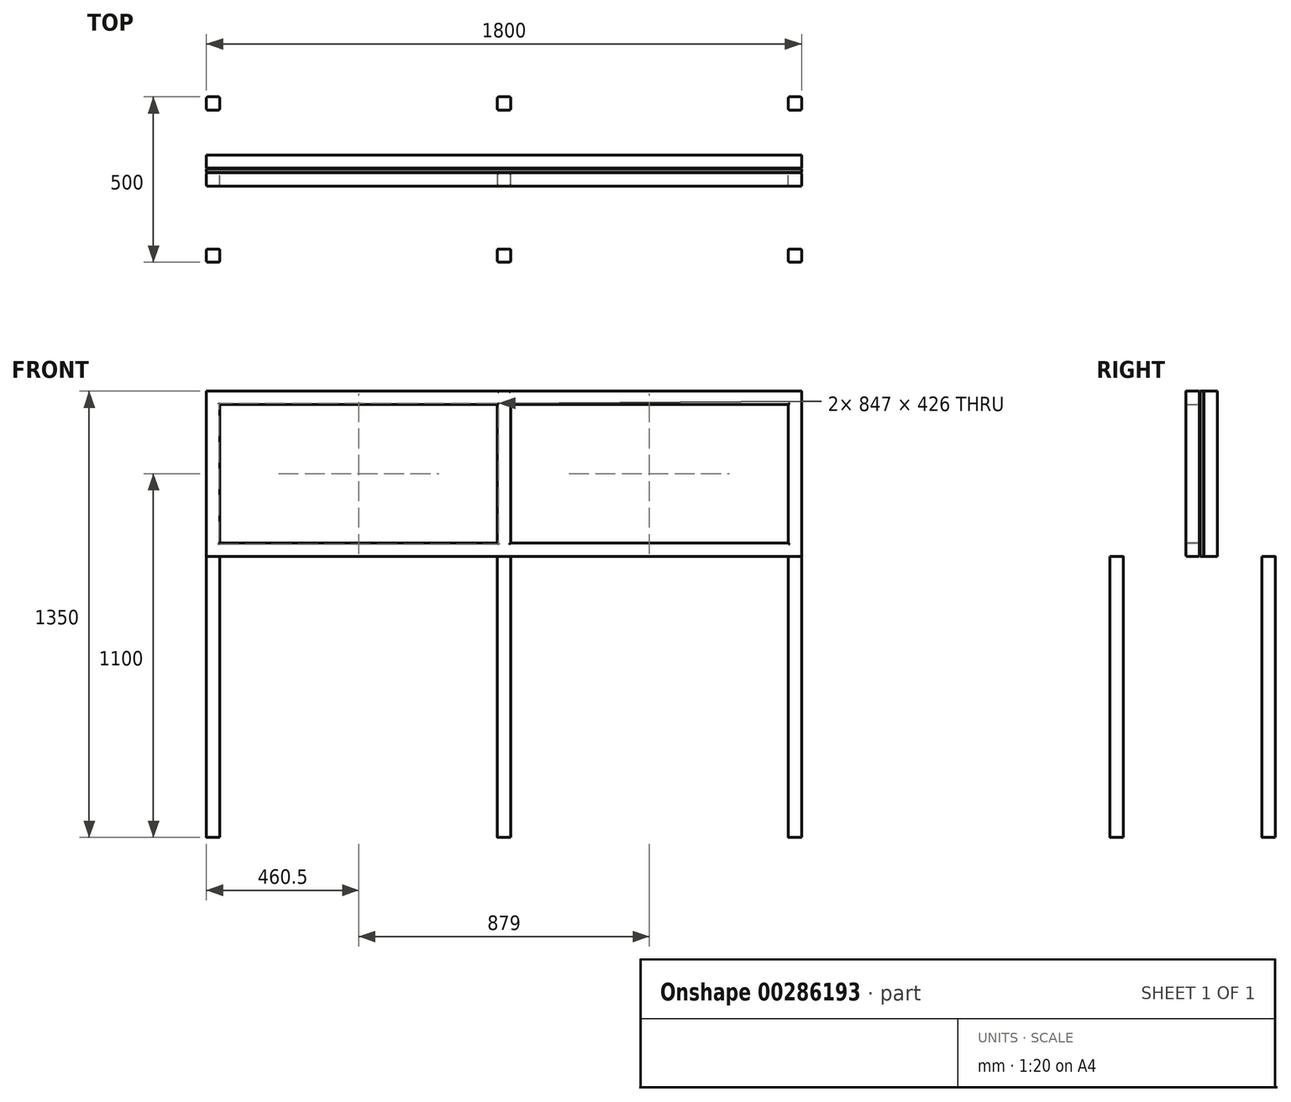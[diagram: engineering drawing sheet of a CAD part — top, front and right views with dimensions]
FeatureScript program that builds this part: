
annotation { "Feature Type Name" : "Feature", "Feature Type Description" : "" }
export const myFeature = defineFeature(function(context is Context, id is Id, definition is map)
    precondition{}
    {
        {
            var Q0;
            Q0=qCreatedBy(makeId("Front.planeOp"),FACE);
            var sketch = newSketch(context, id + "F6", { "sketchPlane" : qUnion([Q0])});
            skLineSegment(sketch, "E0.bottom", {"start": v(880, -230) * mm, "end": v(-880, -230) * mm});
            skLineSegment(sketch, "E0.top", {"start": v(880, 230) * mm, "end": v(-880, 230) * mm});
            skLineSegment(sketch, "E0.left", {"start": v(880, -230) * mm, "end": v(880, 230) * mm});
            skLineSegment(sketch, "E0.right", {"start": v(-880, -230) * mm, "end": v(-880, 230) * mm});
            skPoint(sketch, "E0.middle", {"position": v(0, 0) * mm});
            skLineSegment(sketch, "E1", {"start": v(0, 230) * mm, "end": v(0, -230) * mm});
            skSolve(sketch);
        }
        {
            var Q0;
            Q0=qCreatedBy(makeId("Right.planeOp"),FACE);
            var sketch = newSketch(context, id + "F0", { "sketchPlane" : qUnion([Q0])});
            skLineSegment(sketch, "E2.bottom", {"start": v(17, -250) * mm, "end": v(-17, -250) * mm});
            skLineSegment(sketch, "E2.top", {"start": v(17, -210) * mm, "end": v(-17, -210) * mm});
            skLineSegment(sketch, "E2.left", {"start": v(20, -247) * mm, "end": v(20, -213) * mm});
            skLineSegment(sketch, "E2.right", {"start": v(-20, -247) * mm, "end": v(-20, -213) * mm});
            skPoint(sketch, "E2.middle", {"position": v(0, -230) * mm});
            skPoint(sketch, "E3.visualSharp", {"position": v(20, -210) * mm});
            skArc(sketch, "E3.filletArc", {"start": v(20, -213) * mm, "mid": v(19.12, -210.88) * mm, "end": v(17, -210) * mm});
            skPoint(sketch, "E4.visualSharp", {"position": v(-20, -210) * mm});
            skArc(sketch, "E4.filletArc", {"start": v(-17, -210) * mm, "mid": v(-19.12, -210.88) * mm, "end": v(-20, -213) * mm});
            skPoint(sketch, "E5.visualSharp", {"position": v(20, -250) * mm});
            skArc(sketch, "E5.filletArc", {"start": v(17, -250) * mm, "mid": v(19.12, -249.12) * mm, "end": v(20, -247) * mm});
            skPoint(sketch, "E6.visualSharp", {"position": v(-20, -250) * mm});
            skArc(sketch, "E6.filletArc", {"start": v(-20, -247) * mm, "mid": v(-19.12, -249.12) * mm, "end": v(-17, -250) * mm});
            skSolve(sketch);
        }
        {
            var Q0;
            Q0=makeQuery(id+"F0.imprint","IMPRINT",FACE,{"disambiguationData":[TD([[makeQuery(id+"F0.imprint","IMPRINT",EDGE,{"derivedFrom":sQuery(id+"F0.wireOp",EDGE,"E2.bottom")}),-1.0]])]});
            var Q1;
            Q1=sQuery(id+"F6.wireOp",EDGE,"E0.right");
            var Q2;
            Q2=sQuery(id+"F6.wireOp",EDGE,"E0.top");
            var Q3;
            Q3=sQuery(id+"F6.wireOp",EDGE,"E0.bottom");
            var Q4;
            Q4=sQuery(id+"F6.wireOp",EDGE,"E0.left");
            sweep(context, id + "F7", {"profiles" : qUnion([Q0]), "path" : qUnion([Q1, Q2, Q3, Q4])});
        }
        {
            var Q0;
            Q0=makeQuery(id+"F7.opSweep","SWEPT_FACE",FACE,{"disambiguationData":[OSD([sQuery(id+"F6.wireOp",EDGE,"E0.bottom"),sQuery(id+"F0.wireOp",EDGE,"E2.right")])]});
            var sketch = newSketch(context, id + "F8", { "sketchPlane" : qUnion([Q0])});
            skLineSegment(sketch, "E7.bottom", {"start": v(864, 210) * mm, "end": v(896, 210) * mm});
            skLineSegment(sketch, "E7.top", {"start": v(864, 250) * mm, "end": v(896, 250) * mm});
            skLineSegment(sketch, "E7.left", {"start": v(860, 214) * mm, "end": v(860, 246) * mm});
            skLineSegment(sketch, "E7.right", {"start": v(900, 214) * mm, "end": v(900, 246) * mm});
            skPoint(sketch, "E8.visualSharp", {"position": v(900, 250) * mm});
            skArc(sketch, "E8.filletArc", {"start": v(900, 246) * mm, "mid": v(898.83, 248.83) * mm, "end": v(896, 250) * mm});
            skPoint(sketch, "E9.visualSharp", {"position": v(860, 250) * mm});
            skArc(sketch, "E9.filletArc", {"start": v(864, 250) * mm, "mid": v(861.17, 248.83) * mm, "end": v(860, 246) * mm});
            skPoint(sketch, "E10.visualSharp", {"position": v(860, 210) * mm});
            skArc(sketch, "E10.filletArc", {"start": v(860, 214) * mm, "mid": v(861.17, 211.17) * mm, "end": v(864, 210) * mm});
            skPoint(sketch, "E11.visualSharp", {"position": v(900, 210) * mm});
            skArc(sketch, "E11.filletArc", {"start": v(896, 210) * mm, "mid": v(898.83, 211.17) * mm, "end": v(900, 214) * mm});
            skArc(sketch, "E12.0.1.0", {"start": v(896, -250) * mm, "mid": v(898.83, -248.83) * mm, "end": v(900, -246) * mm});
            skArc(sketch, "E12.0.1.1", {"start": v(864, -210) * mm, "mid": v(861.17, -211.17) * mm, "end": v(860, -214) * mm});
            skLineSegment(sketch, "E12.0.1.2", {"start": v(860, -246) * mm, "end": v(860, -214) * mm});
            skArc(sketch, "E12.0.1.3", {"start": v(900, -214) * mm, "mid": v(898.83, -211.17) * mm, "end": v(896, -210) * mm});
            skLineSegment(sketch, "E12.0.1.4", {"start": v(864, -250) * mm, "end": v(896, -250) * mm});
            skLineSegment(sketch, "E12.0.1.5", {"start": v(864, -210) * mm, "end": v(896, -210) * mm});
            skArc(sketch, "E12.0.1.6", {"start": v(860, -246) * mm, "mid": v(861.17, -248.83) * mm, "end": v(864, -250) * mm});
            skLineSegment(sketch, "E12.0.1.7", {"start": v(900, -246) * mm, "end": v(900, -214) * mm});
            skArc(sketch, "E12.1.0.0", {"start": v(16, 210) * mm, "mid": v(18.83, 211.17) * mm, "end": v(20, 214) * mm});
            skArc(sketch, "E12.1.0.1", {"start": v(-16, 250) * mm, "mid": v(-18.83, 248.83) * mm, "end": v(-20, 246) * mm});
            skLineSegment(sketch, "E12.1.0.2", {"start": v(-20, 214) * mm, "end": v(-20, 246) * mm});
            skArc(sketch, "E12.1.0.3", {"start": v(20, 246) * mm, "mid": v(18.83, 248.83) * mm, "end": v(16, 250) * mm});
            skLineSegment(sketch, "E12.1.0.4", {"start": v(-16, 210) * mm, "end": v(16, 210) * mm});
            skLineSegment(sketch, "E12.1.0.5", {"start": v(-16, 250) * mm, "end": v(16, 250) * mm});
            skArc(sketch, "E12.1.0.6", {"start": v(-20, 214) * mm, "mid": v(-18.83, 211.17) * mm, "end": v(-16, 210) * mm});
            skLineSegment(sketch, "E12.1.0.7", {"start": v(20, 214) * mm, "end": v(20, 246) * mm});
            skArc(sketch, "E12.1.1.0", {"start": v(16, -250) * mm, "mid": v(18.83, -248.83) * mm, "end": v(20, -246) * mm});
            skArc(sketch, "E12.1.1.1", {"start": v(-16, -210) * mm, "mid": v(-18.83, -211.17) * mm, "end": v(-20, -214) * mm});
            skLineSegment(sketch, "E12.1.1.2", {"start": v(-20, -246) * mm, "end": v(-20, -214) * mm});
            skArc(sketch, "E12.1.1.3", {"start": v(20, -214) * mm, "mid": v(18.83, -211.17) * mm, "end": v(16, -210) * mm});
            skLineSegment(sketch, "E12.1.1.4", {"start": v(-16, -250) * mm, "end": v(16, -250) * mm});
            skLineSegment(sketch, "E12.1.1.5", {"start": v(-16, -210) * mm, "end": v(16, -210) * mm});
            skArc(sketch, "E12.1.1.6", {"start": v(-20, -246) * mm, "mid": v(-18.83, -248.83) * mm, "end": v(-16, -250) * mm});
            skLineSegment(sketch, "E12.1.1.7", {"start": v(20, -246) * mm, "end": v(20, -214) * mm});
            skLineSegment(sketch, "E12.direction1", {"start": v(860, 214) * mm, "end": v(-20, 214) * mm, "construction": true});
            skLineSegment(sketch, "E12.direction2", {"start": v(860, 214) * mm, "end": v(860, -246) * mm, "construction": true});
            skArc(sketch, "E13.0.2.0", {"start": v(-864, 210) * mm, "mid": v(-861.17, 211.17) * mm, "end": v(-860, 214) * mm});
            skArc(sketch, "E13.4.2.0", {"start": v(-896, 250) * mm, "mid": v(-898.83, 248.83) * mm, "end": v(-900, 246) * mm});
            skLineSegment(sketch, "E13.8.2.0", {"start": v(-900, 214) * mm, "end": v(-900, 246) * mm});
            skArc(sketch, "E13.11.2.0", {"start": v(-860, 246) * mm, "mid": v(-861.17, 248.83) * mm, "end": v(-864, 250) * mm});
            skLineSegment(sketch, "E13.15.2.0", {"start": v(-896, 210) * mm, "end": v(-864, 210) * mm});
            skLineSegment(sketch, "E13.18.2.0", {"start": v(-896, 250) * mm, "end": v(-864, 250) * mm});
            skArc(sketch, "E13.21.2.0", {"start": v(-900, 214) * mm, "mid": v(-898.83, 211.17) * mm, "end": v(-896, 210) * mm});
            skLineSegment(sketch, "E13.25.2.0", {"start": v(-860, 214) * mm, "end": v(-860, 246) * mm});
            skArc(sketch, "E13.0.2.1", {"start": v(-864, -250) * mm, "mid": v(-861.17, -248.83) * mm, "end": v(-860, -246) * mm});
            skArc(sketch, "E13.4.2.1", {"start": v(-896, -210) * mm, "mid": v(-898.83, -211.17) * mm, "end": v(-900, -214) * mm});
            skLineSegment(sketch, "E13.8.2.1", {"start": v(-900, -246) * mm, "end": v(-900, -214) * mm});
            skArc(sketch, "E13.11.2.1", {"start": v(-860, -214) * mm, "mid": v(-861.17, -211.17) * mm, "end": v(-864, -210) * mm});
            skLineSegment(sketch, "E13.15.2.1", {"start": v(-896, -250) * mm, "end": v(-864, -250) * mm});
            skLineSegment(sketch, "E13.18.2.1", {"start": v(-896, -210) * mm, "end": v(-864, -210) * mm});
            skArc(sketch, "E13.21.2.1", {"start": v(-900, -246) * mm, "mid": v(-898.83, -248.83) * mm, "end": v(-896, -250) * mm});
            skLineSegment(sketch, "E13.25.2.1", {"start": v(-860, -246) * mm, "end": v(-860, -214) * mm});
            skSolve(sketch);
        }
        {
            var Q0;
            Q0 = qSketchRegion(id + "F8", true);
            extrude(context, id + "F1", {"entities" : qUnion([Q0]), "operationType" : NewBodyOperationType.ADD, "depth" : 850 * mm});
        }
        {
            var Q0;
            Q0=makeQuery(id+"F7.opSweep","SWEPT_FACE",FACE,{"disambiguationData":[OSD([sQuery(id+"F6.wireOp",EDGE,"E0.top"),sQuery(id+"F0.wireOp",EDGE,"E2.bottom")])]});
            var sketch = newSketch(context, id + "F9", { "sketchPlane" : qUnion([Q0])});
            skLineSegment(sketch, "E14.bottom", {"start": v(-16, 20) * mm, "end": v(16, 20) * mm});
            skLineSegment(sketch, "E14.top", {"start": v(-16, -20) * mm, "end": v(16, -20) * mm});
            skLineSegment(sketch, "E14.left", {"start": v(-20, 16) * mm, "end": v(-20, -16) * mm});
            skLineSegment(sketch, "E14.right", {"start": v(20, 16) * mm, "end": v(20, -16) * mm});
            skPoint(sketch, "E15.visualSharp", {"position": v(-20, 20) * mm});
            skArc(sketch, "E15.filletArc", {"start": v(-16, 20) * mm, "mid": v(-18.83, 18.83) * mm, "end": v(-20, 16) * mm});
            skPoint(sketch, "E16.visualSharp", {"position": v(20, 20) * mm});
            skArc(sketch, "E16.filletArc", {"start": v(20, 16) * mm, "mid": v(18.83, 18.83) * mm, "end": v(16, 20) * mm});
            skPoint(sketch, "E17.visualSharp", {"position": v(-20, -20) * mm});
            skArc(sketch, "E17.filletArc", {"start": v(-20, -16) * mm, "mid": v(-18.83, -18.83) * mm, "end": v(-16, -20) * mm});
            skPoint(sketch, "E18.visualSharp", {"position": v(20, -20) * mm});
            skArc(sketch, "E18.filletArc", {"start": v(16, -20) * mm, "mid": v(18.83, -18.83) * mm, "end": v(20, -16) * mm});
            skSolve(sketch);
        }
        {
            var Q0;
            Q0 = qSketchRegion(id + "F9", true);
            extrude(context, id + "F10", {"entities" : qUnion([Q0]), "operationType" : NewBodyOperationType.ADD, "oppositeDirection" : true, "depth" : 463.04 * mm});
        }
        {
            var Q0;
            Q0=makeQuery(id+"F7.opSweep","SWEPT_FACE",FACE,{"disambiguationData":[OSD([sQuery(id+"F6.wireOp",EDGE,"E0.left"),sQuery(id+"F0.wireOp",EDGE,"E2.bottom")])]});
            var sketch = newSketch(context, id + "F2", { "sketchPlane" : qUnion([Q0])});
            skLineSegment(sketch, "E19.bottom", {"start": v(22.5, 250) * mm, "end": v(32.5, 250) * mm});
            skLineSegment(sketch, "E19.top", {"start": v(22.5, -250) * mm, "end": v(32.5, -250) * mm});
            skLineSegment(sketch, "E19.left", {"start": v(22.5, 250) * mm, "end": v(22.5, -250) * mm});
            skLineSegment(sketch, "E19.right", {"start": v(32.5, 250) * mm, "end": v(32.5, -250) * mm});
            skSolve(sketch);
        }
        {
            var Q0;
            Q0 = qSketchRegion(id + "F2", true);
            extrude(context, id + "F3", {"entities" : qUnion([Q0]), "operationType" : NewBodyOperationType.ADD, "oppositeDirection" : true, "depth" : 1800 * mm});
        }
        {
            var Q0;
            Q0=makeQuery(id+"F3.opExtrude","CAP_FACE",FACE,{"disambiguationData":[OSD([sQuery(id+"F2.wireOp",EDGE,"E19.bottom"),sQuery(id+"F2.wireOp",EDGE,"E19.top"),sQuery(id+"F2.wireOp",EDGE,"E19.left"),sQuery(id+"F2.wireOp",EDGE,"E19.right")])],"isStart":true});
            var sketch = newSketch(context, id + "F4", { "sketchPlane" : qUnion([Q0])});
            skLineSegment(sketch, "E20.bottom", {"start": v(34.5, 250) * mm, "end": v(74.5, 250) * mm});
            skLineSegment(sketch, "E20.top", {"start": v(34.5, -250) * mm, "end": v(74.5, -250) * mm});
            skLineSegment(sketch, "E20.left", {"start": v(34.5, 250) * mm, "end": v(34.5, -250) * mm});
            skLineSegment(sketch, "E20.right", {"start": v(74.5, 250) * mm, "end": v(74.5, -250) * mm});
            skLineSegment(sketch, "E21.0", {"start": v(32.5, 250) * mm, "end": v(32.5, -250) * mm});
            skSolve(sketch);
        }
        {
            var Q0;
            Q0 = qSketchRegion(id + "F4", true);
            extrude(context, id + "F5", {"entities" : qUnion([Q0]), "oppositeDirection" : true, "depth" : 1800 * mm});
        }
    });
